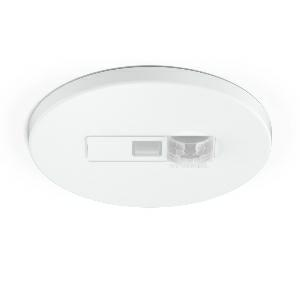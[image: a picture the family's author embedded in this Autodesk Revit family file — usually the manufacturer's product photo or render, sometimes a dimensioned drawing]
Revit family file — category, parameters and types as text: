
# Revit family: ir_micro_057732
name_source: partatom
category: Elektroinstallationen
revit_build: Autodesk Revit 2016 (Build: 20190508_0715(x64)
units: mm (PartAtom-declared; Revit-internal decimal feet)

## family parameters
Basisbauteil = Fläche
Beim Laden mit Abzugskörper schneiden = Nein
Bemaßung runder Anschluss = Durchmesser verwenden
Beschriftungsausrichtung beibehalten = Nein
Gemeinsam genutzt = Nein
Raumberechnungspunkt = Nein
Teiletyp = Normal

## types (1)
- IR Micro
    Apparent Load = 0 VA
    Beschreibung = Type: Presence detector; Dimensions (Ø x H): 80 x 21 mm; Mains power supply: 12 – 22,5 V; Sensor Technology: passive infrared; Application, place: Indoors; Application, room: one-person office, hotel room, care room, function room / ancillary room, WC / washroom, Indoors; Installation site: ceiling; Installation: Concealed wiring; Switching zones: 168 switching zones; Electronic scalability: No; Mechanical scalability: No; Mounting height: 2,00 – 5,00 m; Optimum mounting height: 2,8 m; Detection angle: 360 °; Angle of aperture: 160 °; Sneak-by guard: Yes; Reach, radial: 4 x 4 m (16 m²); Reach, tangential: 6 x 6 m (36 m²); Reach, presence: 4 x 4 m (16 m²); Twilight setting TEACH: Yes; Twilight setting: 2 – 1000 lx; Switching output 1, floating: No; Control output, Dali: Addressable/slave; Basic light level function: No; With bus coupling: Yes; Settings via: Bus; Interconnection: Yes; IP-rating: IP20; Material: Plastic; Ambient temperature: 0 – 40 °C; Colour: white; Colour, RAL: 9003; Manufacturer's Warranty: 5 years; Version: DALI-2 Input Device; PU1, EAN: 4007841057732
    Height = 0 mm  [stored 0 ft]
    Hersteller = Steinel
    Length = 80 mm  [stored 0.262467 ft]
    ModVariant = Nein
    Modell = 057732
    Mounting Place = Ceiling
    Mounting Type = Recessed
    Number of Poles = 1
    OnlyDefault = Ja
    Power Factor = 1
    Product Name = IR Micro
    Product group = Presence detector
    ProductGroupID = 4
    Protection Class = Protection class
    Protection Degree = IP 20
    RlxData = <blob elided: 40177 chars, md5=16cd4fa3>
    SensorDataFile = {"IESDataFiles":[]}
    Typenbild = produkt1_057732.jpg
    Typenkommentare = Product without accessories
    URL = http://relux.com
    VarID = ---
    Voltage = 0 V
    Vorgabe-Ansicht = 1800 mm
    Weight = 0.00 kg
    Width = 0 mm  [stored 0 ft]

note: [stored X ft] marks values corroborated as IEEE doubles in the binary element streams (Revit-internal decimal feet)

## geometry (parser evidence)
native form markers: Sweep x12
no freeform markers — native parametric forms only
